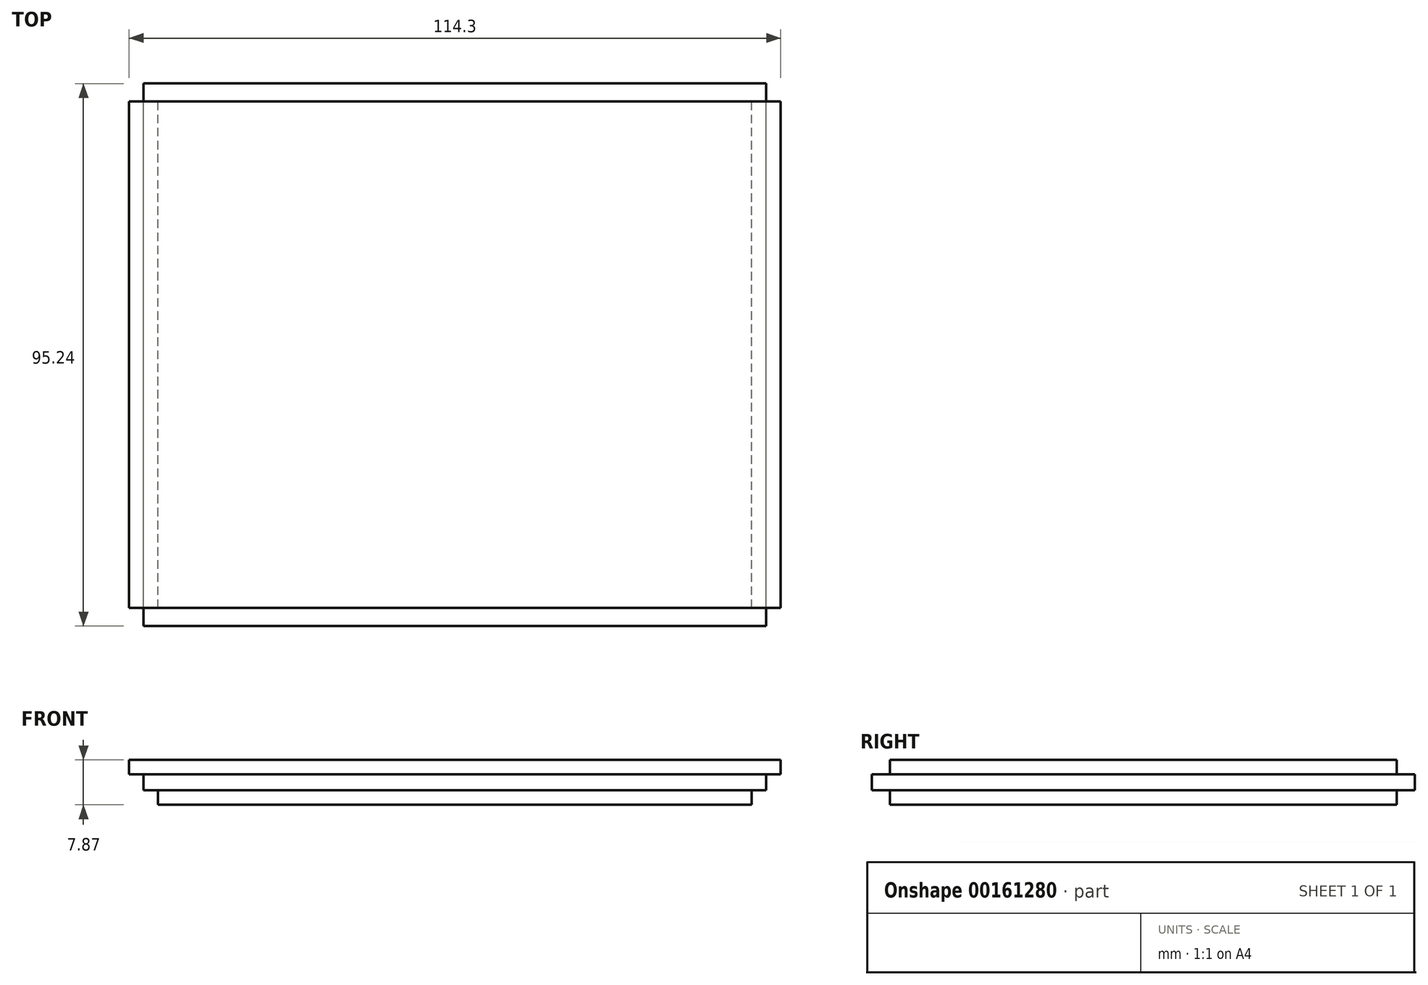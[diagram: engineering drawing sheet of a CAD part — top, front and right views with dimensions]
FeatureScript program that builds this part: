
annotation { "Feature Type Name" : "Feature", "Feature Type Description" : "" }
export const myFeature = defineFeature(function(context is Context, id is Id, definition is map)
    precondition{}
    {
        {
            var Q0;
            Q0=qCreatedBy(makeId("Top.planeOp"),FACE);
            var sketch = newSketch(context, id + "F0", { "sketchPlane" : qUnion([Q0])});
            skLineSegment(sketch, "E0.bottom", {"start": v(57.15, 44.45) * mm, "end": v(-57.15, 44.45) * mm});
            skLineSegment(sketch, "E0.top", {"start": v(57.15, -44.45) * mm, "end": v(-57.15, -44.45) * mm});
            skLineSegment(sketch, "E0.left", {"start": v(57.15, 44.45) * mm, "end": v(57.15, -44.45) * mm});
            skLineSegment(sketch, "E0.right", {"start": v(-57.15, 44.45) * mm, "end": v(-57.15, -44.45) * mm});
            skPoint(sketch, "E0.middle", {"position": v(0, 0) * mm});
            skSolve(sketch);
        }
        {
            var Q0;
            Q0=makeQuery(id+"F0.imprint","IMPRINT",FACE,{"disambiguationData":[TD([[makeQuery(id+"F0.imprint","IMPRINT",EDGE,{"derivedFrom":sQuery(id+"F0.wireOp",EDGE,"E0.bottom")}),1.0]])]});
            extrude(context, id + "F1", {"entities" : qUnion([Q0]), "oppositeDirection" : true, "depth" : 2.54 * mm});
        }
        {
            var Q0;
            Q0=makeQuery(id+"F1.opExtrude","CAP_FACE",FACE,{"disambiguationData":[OSD([sQuery(id+"F0.wireOp",EDGE,"E0.bottom"),sQuery(id+"F0.wireOp",EDGE,"E0.top"),sQuery(id+"F0.wireOp",EDGE,"E0.left"),sQuery(id+"F0.wireOp",EDGE,"E0.right")])],"isStart":false});
            var sketch = newSketch(context, id + "F2", { "sketchPlane" : qUnion([Q0])});
            skLineSegment(sketch, "E1.bottom", {"start": v(54.61, 47.63) * mm, "end": v(-54.61, 47.63) * mm});
            skLineSegment(sketch, "E1.top", {"start": v(54.61, -47.63) * mm, "end": v(-54.61, -47.63) * mm});
            skLineSegment(sketch, "E1.left", {"start": v(54.61, 47.63) * mm, "end": v(54.61, -47.63) * mm});
            skLineSegment(sketch, "E1.right", {"start": v(-54.61, 47.63) * mm, "end": v(-54.61, -47.63) * mm});
            skPoint(sketch, "E1.middle", {"position": v(0, 0) * mm});
            skSolve(sketch);
        }
        {
            var Q0;
            {var subQ0=sQuery(id+"F2.wireOp",EDGE,"E1.bottom");Q0=makeQuery(id+"F2.imprint","IMPRINT",FACE,{"disambiguationData":[TD([[makeQuery(id+"F2.imprint","IMPRINT",EDGE,{"derivedFrom":subQ0}),1.0]])]});}
            var Q1;
            {var subQ0=sQuery(id+"F2.wireOp",EDGE,"E1.left");var subQ1=makeQuery(id+"F1.opExtrude","CAP_EDGE",EDGE,{"disambiguationData":[OSD([sQuery(id+"F0.wireOp",EDGE,"E0.top")])],"isStart":false});var subQ2=makeQuery(id+"F2.imprint","INTERSECT",VERTEX,{"derivedFrom":[subQ1,subQ0]});Q1=makeQuery(id+"F2.imprint","IMPRINT",FACE,{"disambiguationData":[TD([[makeQuery(id+"F2.imprint","IMPRINT",EDGE,{"disambiguationData":[TD([[subQ2,-1.0]])],"derivedFrom":subQ0}),-1.0]])]});}
            var Q2;
            {var subQ0=sQuery(id+"F2.wireOp",EDGE,"E1.top");Q2=makeQuery(id+"F2.imprint","IMPRINT",FACE,{"disambiguationData":[TD([[makeQuery(id+"F2.imprint","IMPRINT",EDGE,{"derivedFrom":subQ0}),-1.0]])]});}
            extrude(context, id + "F3", {"entities" : qUnion([Q0, Q1, Q2]), "operationType" : NewBodyOperationType.ADD, "depth" : 2.8 * mm});
        }
        {
            var Q0;
            Q0=makeQuery(id+"F3.opExtrude","CAP_FACE",FACE,{"disambiguationData":[OSD([sQuery(id+"F2.wireOp",EDGE,"E1.bottom"),sQuery(id+"F2.wireOp",EDGE,"E1.top"),sQuery(id+"F2.wireOp",EDGE,"E1.left"),sQuery(id+"F2.wireOp",EDGE,"E1.right")])],"isStart":false});
            var sketch = newSketch(context, id + "F4", { "sketchPlane" : qUnion([Q0])});
            skLineSegment(sketch, "E2.bottom", {"start": v(52.07, 44.45) * mm, "end": v(-52.07, 44.45) * mm});
            skLineSegment(sketch, "E2.top", {"start": v(52.07, -44.45) * mm, "end": v(-52.07, -44.45) * mm});
            skLineSegment(sketch, "E2.left", {"start": v(52.07, 44.45) * mm, "end": v(52.07, -44.45) * mm});
            skLineSegment(sketch, "E2.right", {"start": v(-52.07, 44.45) * mm, "end": v(-52.07, -44.45) * mm});
            skPoint(sketch, "E2.middle", {"position": v(0, 0) * mm});
            skSolve(sketch);
        }
        {
            var Q0;
            Q0=makeQuery(id+"F4.imprint","IMPRINT",FACE,{"disambiguationData":[TD([[makeQuery(id+"F4.imprint","IMPRINT",EDGE,{"derivedFrom":sQuery(id+"F4.wireOp",EDGE,"E2.bottom")}),1.0]])]});
            extrude(context, id + "F5", {"entities" : qUnion([Q0]), "operationType" : NewBodyOperationType.ADD, "depth" : 2.54 * mm});
        }
    });
